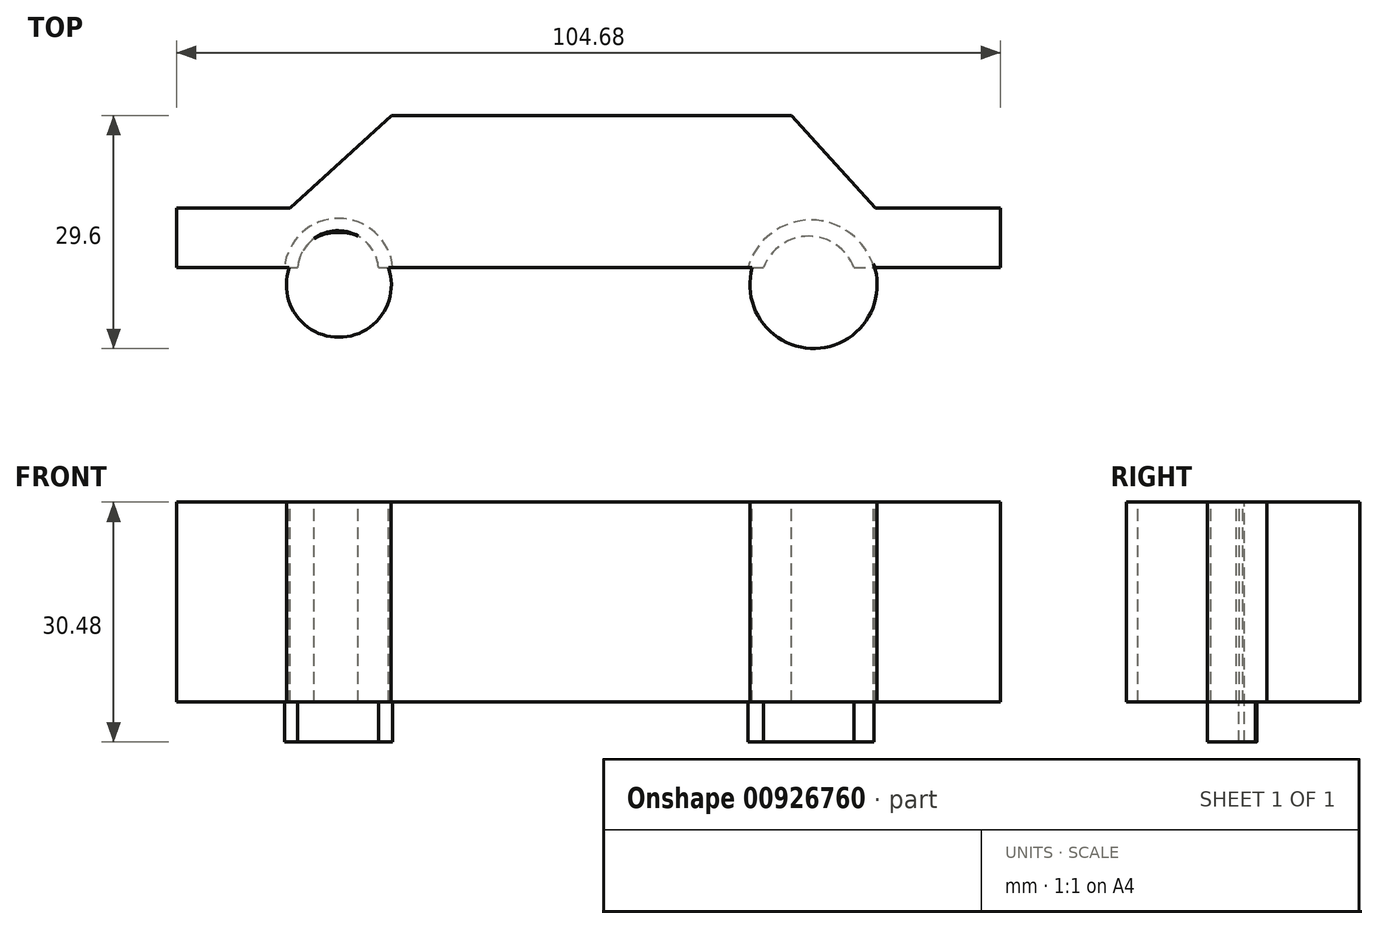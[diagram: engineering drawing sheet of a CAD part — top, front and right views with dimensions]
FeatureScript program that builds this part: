
annotation { "Feature Type Name" : "Feature", "Feature Type Description" : "" }
export const myFeature = defineFeature(function(context is Context, id is Id, definition is map)
    precondition{}
    {
        {
            var Q0;
            Q0=qCreatedBy(makeId("Top.planeOp"),FACE);
            var sketch = newSketch(context, id + "F0", { "sketchPlane" : qUnion([Q0])});
            skLineSegment(sketch, "E0", {"start": v(-51.4, 0) * mm, "end": v(-51.4, 7.59) * mm});
            skLineSegment(sketch, "E1", {"start": v(-51.4, 7.59) * mm, "end": v(-36.98, 7.59) * mm});
            skLineSegment(sketch, "E2", {"start": v(-36.98, 7.59) * mm, "end": v(-24.08, 19.34) * mm});
            skLineSegment(sketch, "E3", {"start": v(-24.08, 19.34) * mm, "end": v(26.74, 19.34) * mm});
            skLineSegment(sketch, "E4", {"start": v(26.74, 19.34) * mm, "end": v(37.36, 7.59) * mm});
            skLineSegment(sketch, "E5", {"start": v(37.36, 7.59) * mm, "end": v(53.29, 7.59) * mm});
            skLineSegment(sketch, "E6", {"start": v(53.29, 7.59) * mm, "end": v(53.29, 0) * mm});
            skLineSegment(sketch, "E7", {"start": v(53.29, 0) * mm, "end": v(37.36, 0) * mm});
            skLineSegment(sketch, "E8", {"start": v(21.8, 0) * mm, "end": v(-24.08, 0) * mm});
            skLineSegment(sketch, "E9", {"start": v(-51.4, 0) * mm, "end": v(-36.98, 0) * mm});
            skArc(sketch, "E10", {"start": v(-24.08, 0) * mm, "mid": v(-30.53, 4.94) * mm, "end": v(-36.98, 0) * mm});
            skArc(sketch, "E11", {"start": v(37.36, 0) * mm, "mid": v(29.58, 5.31) * mm, "end": v(21.8, 0) * mm});
            skPoint(sketch, "E11.midSnap0", {"position": v(32.05, 13.46) * mm});
            skPoint(sketch, "E11.midSnap1", {"position": v(-30.53, 4.94) * mm});
            skSolve(sketch);
        }
        {
            var Q0;
            Q0=makeQuery(id+"F0.imprint","IMPRINT",FACE,{"disambiguationData":[TD([[makeQuery(id+"F0.imprint","IMPRINT",EDGE,{"derivedFrom":sQuery(id+"F0.wireOp",EDGE,"E0")}),-1.0]])]});
            extrude(context, id + "F1", {"entities" : qUnion([Q0]), "oppositeDirection" : true, "depth" : 25.4 * mm, "offsetDistance" : 25.4 * mm});
        }
        {
            var Q0;
            Q0=qCreatedBy(makeId("Top.planeOp"),FACE);
            var sketch = newSketch(context, id + "F2", { "sketchPlane" : qUnion([Q0])});
            skCircle(sketch, "E12", {"center": v(-30.78, -2.16) * mm, "radius": 6.67 * mm});
            skPoint(sketch, "E12.first.point", {"position": v(-37.08, 0) * mm});
            skPoint(sketch, "E12.second.point", {"position": v(-24.21, -3.33) * mm});
            skPoint(sketch, "E12.third.point", {"position": v(-24.47, 0) * mm});
            skCircle(sketch, "E13", {"center": v(29.52, -2.17) * mm, "radius": 8.08 * mm});
            skPoint(sketch, "E13.first.point", {"position": v(21.73, 0) * mm});
            skPoint(sketch, "E13.second.point", {"position": v(37.3, 0) * mm});
            skPoint(sketch, "E13.third.point", {"position": v(33.19, -9.38) * mm});
            skSolve(sketch);
        }
        {
            var Q0;
            Q0=makeQuery(id+"F2.imprint","IMPRINT",FACE,{"disambiguationData":[TD([[makeQuery(id+"F2.imprint","IMPRINT",EDGE,{"derivedFrom":sQuery(id+"F2.wireOp",EDGE,"E12")}),1.0]])]});
            var Q1;
            Q1=makeQuery(id+"F2.imprint","IMPRINT",FACE,{"disambiguationData":[TD([[makeQuery(id+"F2.imprint","IMPRINT",EDGE,{"derivedFrom":sQuery(id+"F2.wireOp",EDGE,"E13")}),1.0]])]});
            extrude(context, id + "F3", {"entities" : qUnion([Q0, Q1]), "operationType" : NewBodyOperationType.ADD, "oppositeDirection" : true, "depth" : 25.4 * mm, "offsetDistance" : 25.4 * mm});
        }
        {
            var Q0;
            Q0=qCreatedBy(makeId("Top.planeOp"),FACE);
            var sketch = newSketch(context, id + "F4", { "sketchPlane" : qUnion([Q0])});
            skArc(sketch, "E14", {"start": v(-23.93, 0) * mm, "mid": v(-30.81, 6.26) * mm, "end": v(-37.7, 0) * mm});
            skArc(sketch, "E15", {"start": v(-25.73, 0) * mm, "mid": v(-30.88, 4.71) * mm, "end": v(-36.02, 0) * mm});
            skLineSegment(sketch, "E16", {"start": v(-25.73, 0) * mm, "end": v(-23.93, 0) * mm});
            skLineSegment(sketch, "E17", {"start": v(-37.7, 0) * mm, "end": v(-36.02, 0) * mm});
            skArc(sketch, "E18", {"start": v(37.2, 0) * mm, "mid": v(29.19, 6.07) * mm, "end": v(21.18, 0) * mm});
            skArc(sketch, "E19", {"start": v(34.65, 0) * mm, "mid": v(28.91, 4) * mm, "end": v(23.18, 0) * mm});
            skLineSegment(sketch, "E20", {"start": v(21.18, 0) * mm, "end": v(23.18, 0) * mm});
            skLineSegment(sketch, "E21", {"start": v(34.65, 0) * mm, "end": v(37.2, 0) * mm});
            skSolve(sketch);
        }
        {
            var Q0;
            Q0=makeQuery(id+"F4.imprint","IMPRINT",FACE,{"disambiguationData":[TD([[makeQuery(id+"F4.imprint","IMPRINT",EDGE,{"derivedFrom":sQuery(id+"F4.wireOp",EDGE,"E14")}),1.0]])]});
            var Q1;
            Q1=makeQuery(id+"F4.imprint","IMPRINT",FACE,{"disambiguationData":[TD([[makeQuery(id+"F4.imprint","IMPRINT",EDGE,{"derivedFrom":sQuery(id+"F4.wireOp",EDGE,"E18")}),1.0]])]});
            extrude(context, id + "F5", {"entities" : qUnion([Q0, Q1]), "operationType" : NewBodyOperationType.ADD, "oppositeDirection" : true, "depth" : 30.48 * mm, "offsetDistance" : 25.4 * mm});
        }
    });
